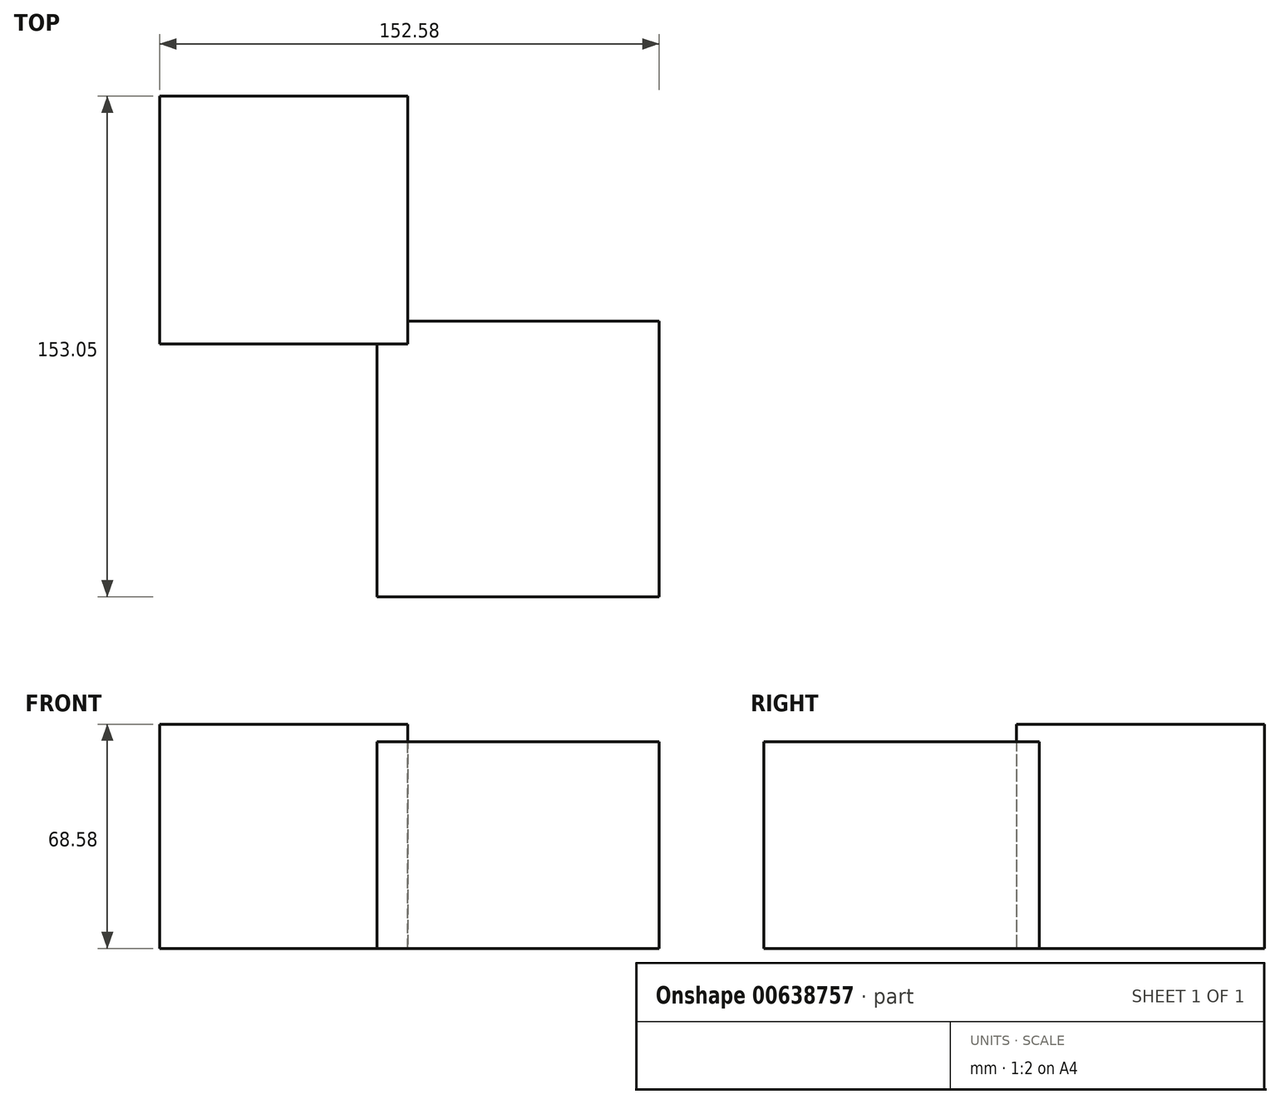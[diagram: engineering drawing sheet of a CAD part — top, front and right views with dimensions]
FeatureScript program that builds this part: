
annotation { "Feature Type Name" : "Feature", "Feature Type Description" : "" }
export const myFeature = defineFeature(function(context is Context, id is Id, definition is map)
    precondition{}
    {
        {
            var Q0;
            Q0=qCreatedBy(makeId("Top.planeOp"),FACE);
            var sketch = newSketch(context, id + "F0", { "sketchPlane" : qUnion([Q0])});
            skLineSegment(sketch, "E0.bottom", {"start": v(0, 0) * mm, "end": v(-75.79, 0) * mm});
            skLineSegment(sketch, "E0.top", {"start": v(0, 75.79) * mm, "end": v(-75.79, 75.79) * mm});
            skLineSegment(sketch, "E0.left", {"start": v(0, 0) * mm, "end": v(0, 75.79) * mm});
            skLineSegment(sketch, "E0.right", {"start": v(-75.79, 0) * mm, "end": v(-75.79, 75.79) * mm});
            skSolve(sketch);
        }
        {
            var Q0;
            Q0 = qSketchRegion(id + "F0", true);
            extrude(context, id + "F1", {"entities" : qUnion([Q0]), "depth" : 68.58 * mm, "offsetDistance" : 25.4 * mm});
        }
        {
            var Q0;
            Q0=qCreatedBy(makeId("Top.planeOp"),FACE);
            var sketch = newSketch(context, id + "F2", { "sketchPlane" : qUnion([Q0])});
            skLineSegment(sketch, "E1.bottom", {"start": v(76.79, -77.26) * mm, "end": v(-9.43, -77.26) * mm});
            skLineSegment(sketch, "E1.top", {"start": v(76.79, 7.05) * mm, "end": v(-9.43, 7.05) * mm});
            skLineSegment(sketch, "E1.left", {"start": v(76.79, -77.26) * mm, "end": v(76.79, 7.05) * mm});
            skLineSegment(sketch, "E1.right", {"start": v(-9.43, -77.26) * mm, "end": v(-9.43, 7.05) * mm});
            skSolve(sketch);
        }
        {
            var Q0;
            Q0=makeQuery(id+"F2.imprint","IMPRINT",FACE,{"disambiguationData":[TD([[makeQuery(id+"F2.imprint","IMPRINT",EDGE,{"derivedFrom":sQuery(id+"F2.wireOp",EDGE,"E1.bottom")}),-1.0]])]});
            extrude(context, id + "F3", {"entities" : qUnion([Q0]), "operationType" : NewBodyOperationType.ADD, "depth" : 63.25 * mm, "offsetDistance" : 25.4 * mm});
        }
    });
